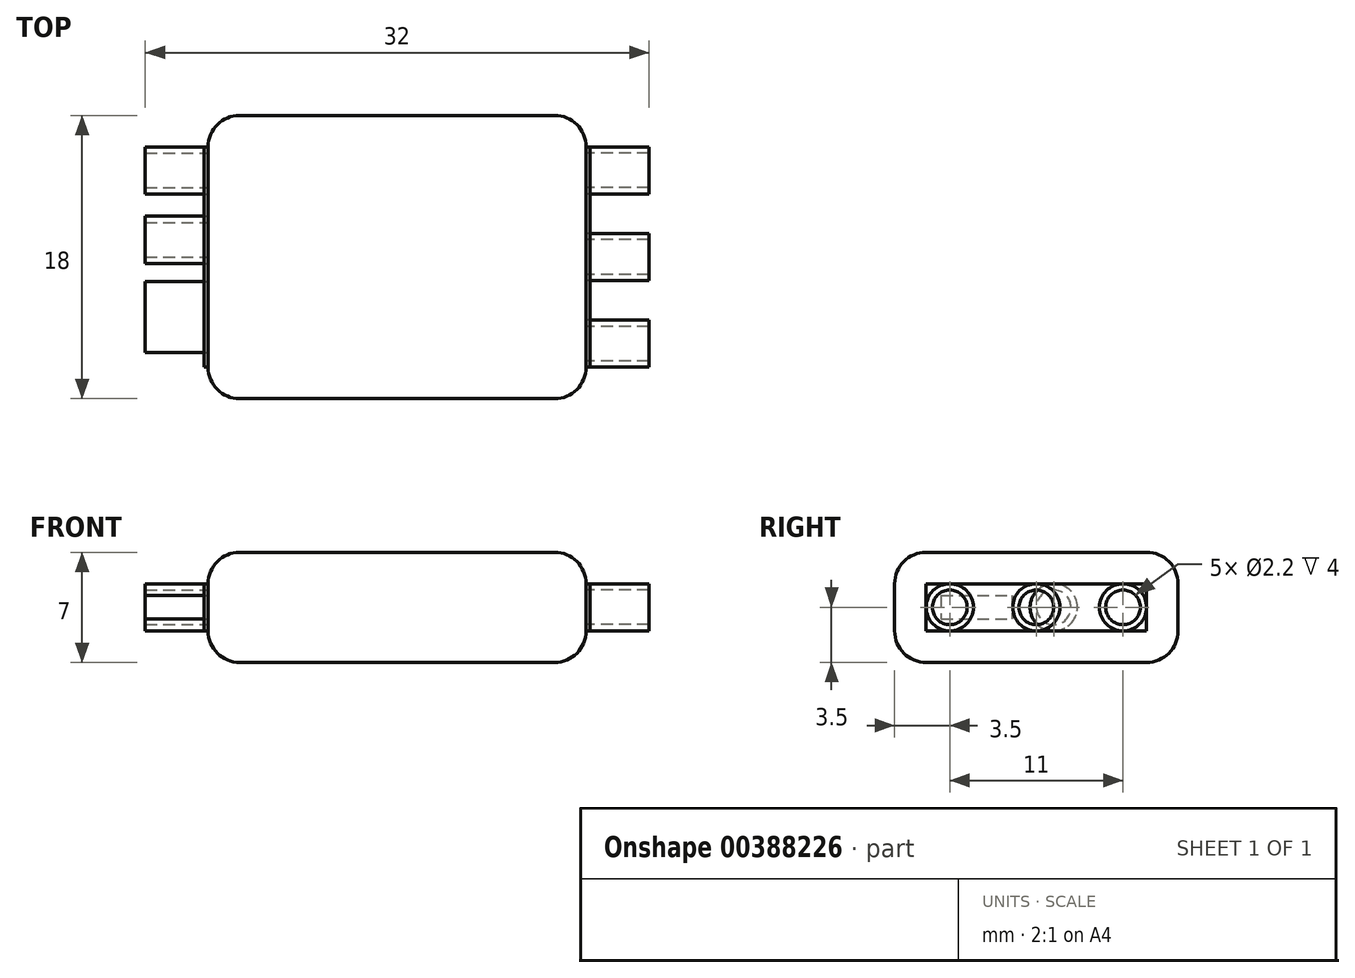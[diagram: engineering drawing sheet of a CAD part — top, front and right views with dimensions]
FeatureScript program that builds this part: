
annotation { "Feature Type Name" : "Feature", "Feature Type Description" : "" }
export const myFeature = defineFeature(function(context is Context, id is Id, definition is map)
    precondition{}
    {
        {
            var Q0;
            Q0=qCreatedBy(makeId("Top.planeOp"),FACE);
            var sketch = newSketch(context, id + "F0", { "sketchPlane" : qUnion([Q0])});
            skLineSegment(sketch, "E0.bottom", {"start": v(10, 9) * mm, "end": v(-10, 9) * mm});
            skLineSegment(sketch, "E0.top", {"start": v(10, -9) * mm, "end": v(-10, -9) * mm});
            skLineSegment(sketch, "E0.left", {"start": v(12, 7) * mm, "end": v(12, -7) * mm});
            skLineSegment(sketch, "E0.right", {"start": v(-12, 7) * mm, "end": v(-12, -7) * mm});
            skPoint(sketch, "E0.middle", {"position": v(0, 0) * mm});
            skPoint(sketch, "E1.visualSharp", {"position": v(-12, 9) * mm});
            skArc(sketch, "E1.filletArc", {"start": v(-10, 9) * mm, "mid": v(-11.41, 8.41) * mm, "end": v(-12, 7) * mm});
            skPoint(sketch, "E2.visualSharp", {"position": v(12, 9) * mm});
            skArc(sketch, "E2.filletArc", {"start": v(12, 7) * mm, "mid": v(11.41, 8.41) * mm, "end": v(10, 9) * mm});
            skPoint(sketch, "E3.visualSharp", {"position": v(12, -9) * mm});
            skArc(sketch, "E3.filletArc", {"start": v(10, -9) * mm, "mid": v(11.41, -8.41) * mm, "end": v(12, -7) * mm});
            skPoint(sketch, "E4.visualSharp", {"position": v(-12, -9) * mm});
            skArc(sketch, "E4.filletArc", {"start": v(-12, -7) * mm, "mid": v(-11.41, -8.41) * mm, "end": v(-10, -9) * mm});
            skSolve(sketch);
        }
        {
            var Q0;
            Q0=makeQuery(id+"F0.imprint","IMPRINT",FACE,{"disambiguationData":[TD([[makeQuery(id+"F0.imprint","IMPRINT",EDGE,{"derivedFrom":sQuery(id+"F0.wireOp",EDGE,"E0.bottom")}),1.0]])]});
            extrude(context, id + "F1", {"entities" : qUnion([Q0]), "depth" : 7 * mm});
        }
        {
            var Q0;
            Q0=makeQuery(id+"F1.opExtrude","CAP_FACE",FACE,{"disambiguationData":[OSD([sQuery(id+"F0.wireOp",EDGE,"E0.bottom"),sQuery(id+"F0.wireOp",EDGE,"E0.top"),sQuery(id+"F0.wireOp",EDGE,"E0.left"),sQuery(id+"F0.wireOp",EDGE,"E0.right"),sQuery(id+"F0.wireOp",EDGE,"E1.filletArc"),sQuery(id+"F0.wireOp",EDGE,"E2.filletArc"),sQuery(id+"F0.wireOp",EDGE,"E3.filletArc"),sQuery(id+"F0.wireOp",EDGE,"E4.filletArc")])],"isStart":false});
            var Q1;
            Q1=makeQuery(id+"F1.opExtrude","CAP_FACE",FACE,{"disambiguationData":[OSD([sQuery(id+"F0.wireOp",EDGE,"E0.bottom"),sQuery(id+"F0.wireOp",EDGE,"E0.top"),sQuery(id+"F0.wireOp",EDGE,"E0.left"),sQuery(id+"F0.wireOp",EDGE,"E0.right"),sQuery(id+"F0.wireOp",EDGE,"E1.filletArc"),sQuery(id+"F0.wireOp",EDGE,"E2.filletArc"),sQuery(id+"F0.wireOp",EDGE,"E3.filletArc"),sQuery(id+"F0.wireOp",EDGE,"E4.filletArc")])],"isStart":true});
            fillet(context, id + "F2", {"entities" : qUnion([Q0, Q1]), "radius" : 2 * mm, "tangentPropagation" : true, "allowEdgeOverflow" : false});
        }
        {
            var Q0;
            Q0=makeQuery(id+"F1.opExtrude","SWEPT_FACE",FACE,{"disambiguationData":[OSD([sQuery(id+"F0.wireOp",EDGE,"E0.left")])]});
            var sketch = newSketch(context, id + "F3", { "sketchPlane" : qUnion([Q0])});
            skLineSegment(sketch, "E5", {"start": v(-7, 3.5) * mm, "end": v(7, 3.5) * mm, "construction": true});
            skCircle(sketch, "E6", {"center": v(0, 3.5) * mm, "radius": 1.1 * mm});
            skCircle(sketch, "E7", {"center": v(0, 3.5) * mm, "radius": 1.5 * mm});
            skCircle(sketch, "E8", {"center": v(5.5, 3.5) * mm, "radius": 1.5 * mm});
            skCircle(sketch, "E9", {"center": v(5.5, 3.5) * mm, "radius": 1.1 * mm});
            skCircle(sketch, "E10", {"center": v(-5.5, 3.5) * mm, "radius": 1.5 * mm});
            skCircle(sketch, "E11", {"center": v(-5.5, 3.5) * mm, "radius": 1.1 * mm});
            skSolve(sketch);
        }
        {
            var Q0;
            Q0=makeQuery(id+"F3.imprint","IMPRINT",FACE,{"disambiguationData":[TD([[makeQuery(id+"F3.imprint","IMPRINT",EDGE,{"derivedFrom":sQuery(id+"F3.wireOp",EDGE,"E11")}),-1.0]])]});
            var Q1;
            Q1=makeQuery(id+"F3.imprint","IMPRINT",FACE,{"disambiguationData":[TD([[makeQuery(id+"F3.imprint","IMPRINT",EDGE,{"derivedFrom":sQuery(id+"F3.wireOp",EDGE,"E6")}),-1.0]])]});
            var Q2;
            Q2=makeQuery(id+"F3.imprint","IMPRINT",FACE,{"disambiguationData":[TD([[makeQuery(id+"F3.imprint","IMPRINT",EDGE,{"derivedFrom":sQuery(id+"F3.wireOp",EDGE,"E9")}),-1.0]])]});
            extrude(context, id + "F4", {"entities" : qUnion([Q0, Q1, Q2]), "depth" : 4 * mm});
        }
        {
            var Q0;
            Q0=makeQuery(id+"F1.opExtrude","SWEPT_FACE",FACE,{"disambiguationData":[OSD([sQuery(id+"F0.wireOp",EDGE,"E0.right")])]});
            var sketch = newSketch(context, id + "F5", { "sketchPlane" : qUnion([Q0])});
            skCircle(sketch, "E12.0", {"center": v(-5.5, 3.5) * mm, "radius": 1.5 * mm});
            skCircle(sketch, "E13.0", {"center": v(-5.5, 3.5) * mm, "radius": 1.1 * mm});
            skCircle(sketch, "E14", {"center": v(-1.1, 3.5) * mm, "radius": 1.5 * mm});
            skCircle(sketch, "E15", {"center": v(-1.1, 3.5) * mm, "radius": 1.1 * mm});
            skLineSegment(sketch, "E16.bottom", {"start": v(6.06, 4.25) * mm, "end": v(1.56, 4.25) * mm});
            skLineSegment(sketch, "E16.top", {"start": v(6.06, 2.75) * mm, "end": v(1.56, 2.75) * mm});
            skLineSegment(sketch, "E16.left", {"start": v(6.06, 4.25) * mm, "end": v(6.06, 2.75) * mm});
            skLineSegment(sketch, "E16.right", {"start": v(1.56, 4.25) * mm, "end": v(1.56, 2.75) * mm});
            skPoint(sketch, "E16.middle", {"position": v(3.8, 3.5) * mm});
            skPoint(sketch, "E16.middle.positionSnap0", {"position": v(7, 3.5) * mm});
            skPoint(sketch, "E16.centerSnap0", {"position": v(7, 3.5) * mm});
            skSolve(sketch);
        }
        {
            var Q0;
            Q0 = qSketchRegion(id + "F5", true);
            extrude(context, id + "F6", {"entities" : qUnion([Q0]), "depth" : 4 * mm});
        }
        {
            var Q0;
            Q0=makeQuery(id+"F1.opExtrude","SWEPT_FACE",FACE,{"disambiguationData":[OSD([sQuery(id+"F0.wireOp",EDGE,"E0.left")])]});
            var sketch = newSketch(context, id + "F7", { "sketchPlane" : qUnion([Q0])});
            skLineSegment(sketch, "E17.bottom", {"start": v(-7, 5) * mm, "end": v(7, 5) * mm});
            skLineSegment(sketch, "E17.top", {"start": v(-7, 2) * mm, "end": v(7, 2) * mm});
            skLineSegment(sketch, "E17.left", {"start": v(-7, 5) * mm, "end": v(-7, 2) * mm});
            skLineSegment(sketch, "E17.right", {"start": v(7, 5) * mm, "end": v(7, 2) * mm});
            skSolve(sketch);
        }
        {
            var Q0;
            Q0 = qSketchRegion(id + "F7", true);
            extrude(context, id + "F8", {"entities" : qUnion([Q0]), "depth" : .25 * mm});
        }
        {
            var Q0;
            Q0=makeQuery(id+"F1.opExtrude","SWEPT_FACE",FACE,{"disambiguationData":[OSD([sQuery(id+"F0.wireOp",EDGE,"E0.right")])]});
            var sketch = newSketch(context, id + "F9", { "sketchPlane" : qUnion([Q0])});
            skLineSegment(sketch, "E18.bottom", {"start": v(-7, 5) * mm, "end": v(7, 5) * mm});
            skLineSegment(sketch, "E18.top", {"start": v(-7, 2) * mm, "end": v(7, 2) * mm});
            skLineSegment(sketch, "E18.left", {"start": v(-7, 5) * mm, "end": v(-7, 2) * mm});
            skLineSegment(sketch, "E18.right", {"start": v(7, 5) * mm, "end": v(7, 2) * mm});
            skSolve(sketch);
        }
        {
            var Q0;
            Q0=makeQuery(id+"F9.imprint","IMPRINT",FACE,{"disambiguationData":[TD([[makeQuery(id+"F9.imprint","IMPRINT",EDGE,{"derivedFrom":sQuery(id+"F9.wireOp",EDGE,"E18.bottom")}),1.0]])]});
            extrude(context, id + "F10", {"entities" : qUnion([Q0]), "depth" : .25 * mm});
        }
    });
